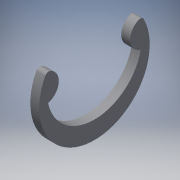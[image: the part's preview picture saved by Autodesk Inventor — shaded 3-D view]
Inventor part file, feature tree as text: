
AUTODESK INVENTOR PART (.ipt)
format: ipt  version: 2017 (Build 210142000, 142)  size: 108,032 bytes
history: native  units: in
note: dims shown in document units (in); Inventor stores cm internally (conversion verified against a paired STEP export)
features: extrude x1
ambient origin geometry x8: Origin, YZ Plane, XZ Plane, XY Plane, X Axis, Y Axis, Z Axis, Center Point
bodies: Solid1 (feature_tree)
feature tree (1):
  extrude  "Extrude1"  [1 undecoded]
note: 1 required parameter value undecoded (feature->parameter linkage not recoverable at this tier; creation-order binding heuristic only, values carry confidence <= 0.55)
